# Revit family: FU_Chair_Sandler_OSWELL 4-4
name_source: partatom
category: Furniture
units: mm (PartAtom-declared; Revit-internal decimal feet)

## family parameters
Always vertical = Yes
Cut with Voids When Loaded = No
OmniClass Number = 23.40.20.00
OmniClass Title = General Furniture and Specialties
Render Appearance Source = Family Geometry
Room Calculation Point = No
Shared = No
Work Plane-Based = No

## types (1)
- Oswell 4.4
    Default Elevation = 0 mm  [stored 0 ft]
    Depth = 530 mm  [stored 1.73885 ft]
    Description = Counter stool with wood legs and a seat pad for added comfort. FSC-certified oak wood, Greenguard Gold-certified.
    Height = 1015 mm  [stored 3.33005 ft]
    Manufacturer = Sandler
    Model = Oswell 4.4
    URL = https://www.sandlerseating.com
    Width = 495 mm  [stored 1.62402 ft]

note: [stored X ft] marks values corroborated as IEEE doubles in the binary element streams (Revit-internal decimal feet)

## geometry (parser evidence)
native form markers: Sweep x11
no freeform markers — native parametric forms only
